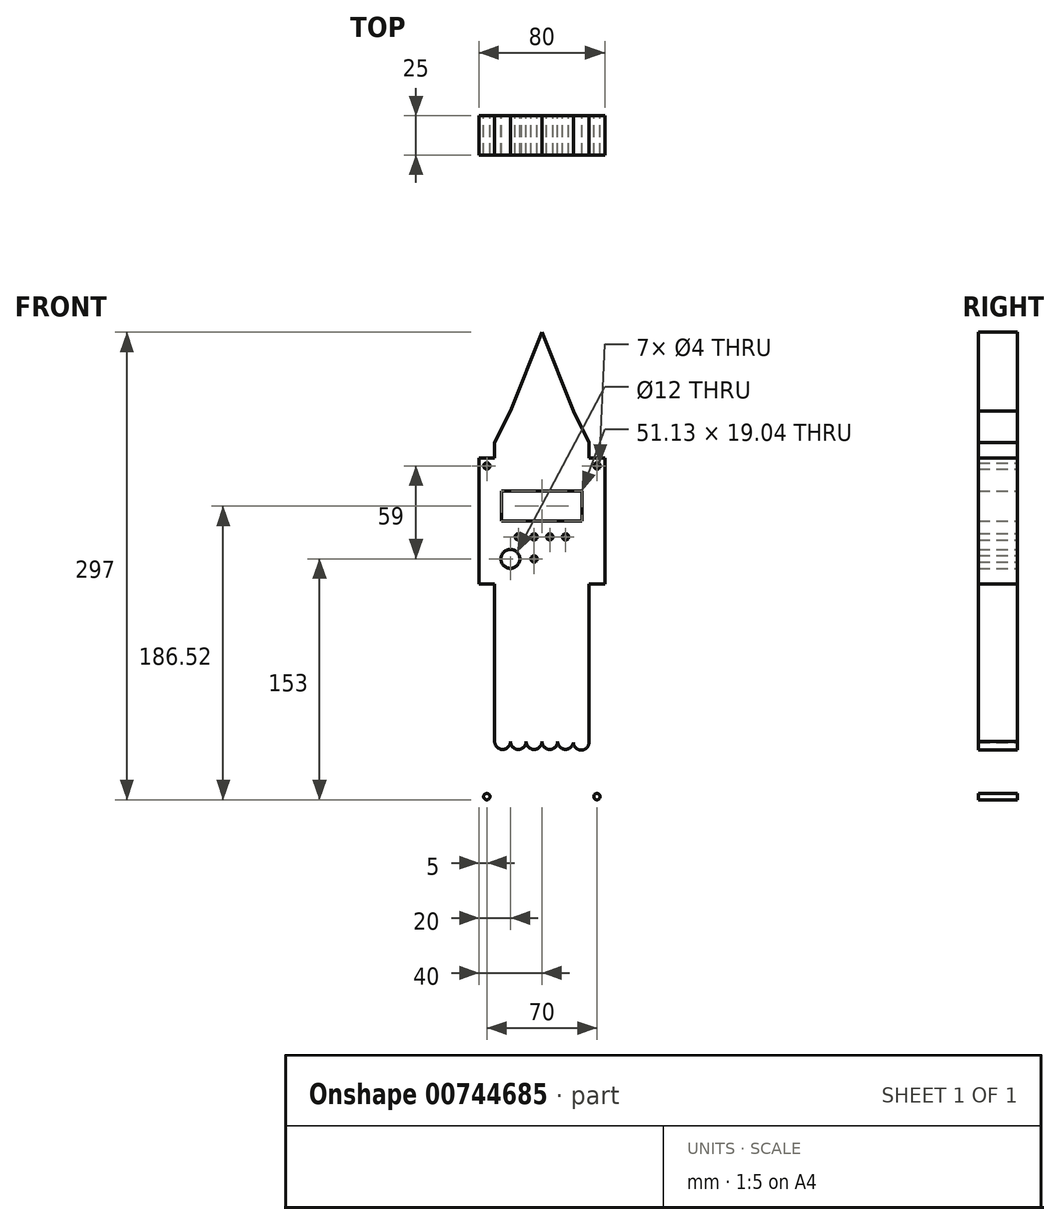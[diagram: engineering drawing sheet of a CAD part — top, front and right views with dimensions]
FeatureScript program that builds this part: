
annotation { "Feature Type Name" : "Feature", "Feature Type Description" : "" }
export const myFeature = defineFeature(function(context is Context, id is Id, definition is map)
    precondition{}
    {
        {
            var Q0;
            Q0=qCreatedBy(makeId("Front.planeOp"),FACE);
            var sketch = newSketch(context, id + "F0", { "sketchPlane" : qUnion([Q0])});
            skLineSegment(sketch, "E0", {"start": v(0, 0) * mm, "end": v(-40, 0) * mm});
            skLineSegment(sketch, "E1", {"start": v(-40, 0) * mm, "end": v(-40, 10) * mm});
            skLineSegment(sketch, "E2", {"start": v(-40, 10) * mm, "end": v(-30, 10) * mm});
            skLineSegment(sketch, "E3", {"start": v(-30, 10) * mm, "end": v(-30, 140) * mm});
            skLineSegment(sketch, "E4", {"start": v(-30, 140) * mm, "end": v(-40, 140) * mm});
            skLineSegment(sketch, "E5", {"start": v(-40, 140) * mm, "end": v(-40, 220) * mm});
            skLineSegment(sketch, "E6", {"start": v(-40, 220) * mm, "end": v(-30, 220) * mm});
            skLineSegment(sketch, "E7", {"start": v(-30, 220) * mm, "end": v(-30, 230) * mm});
            skLineSegment(sketch, "E8", {"start": v(-30, 230) * mm, "end": v(0, 230) * mm});
            skLineSegment(sketch, "E9", {"start": v(0, 250) * mm, "end": v(-20, 250) * mm});
            skLineSegment(sketch, "E10", {"start": v(-30, 230) * mm, "end": v(-20, 250) * mm});
            skLineSegment(sketch, "E11", {"start": v(-20, 250) * mm, "end": v(0, 300) * mm});
            skLineSegment(sketch, "E12.MirrorCS", {"start": v(39.95, 10) * mm, "end": v(29.95, 10) * mm});
            skLineSegment(sketch, "E13.MirrorCS", {"start": v(30, 140) * mm, "end": v(40, 140) * mm});
            skLineSegment(sketch, "E14.MirrorCS", {"start": v(40, 220) * mm, "end": v(30, 220) * mm});
            skLineSegment(sketch, "E15.MirrorCS", {"start": v(30, 220) * mm, "end": v(30, 230) * mm});
            skLineSegment(sketch, "E16.MirrorCS", {"start": v(39.95, 0) * mm, "end": v(39.95, 10) * mm});
            skLineSegment(sketch, "E17.MirrorCS", {"start": v(20, 250) * mm, "end": v(0, 300) * mm});
            skLineSegment(sketch, "E18.MirrorCS", {"start": v(30, 230) * mm, "end": v(20, 250) * mm});
            skLineSegment(sketch, "E19.MirrorCS", {"start": v(-0.05, 0) * mm, "end": v(39.95, 0) * mm});
            skLineSegment(sketch, "E20.MirrorCS", {"start": v(29.95, 10) * mm, "end": v(30, 140) * mm});
            skLineSegment(sketch, "E21.MirrorCS", {"start": v(30, 230) * mm, "end": v(0, 230) * mm});
            skLineSegment(sketch, "E22.MirrorCS", {"start": v(0, 250) * mm, "end": v(20, 250) * mm});
            skLineSegment(sketch, "E23.MirrorCS", {"start": v(40, 140) * mm, "end": v(40, 220) * mm});
            skLineSegment(sketch, "E24", {"start": v(-30, 140) * mm, "end": v(30, 140) * mm});
            skLineSegment(sketch, "E25", {"start": v(-30, 220) * mm, "end": v(30, 220) * mm});
            skLineSegment(sketch, "E26", {"start": v(-20, 140) * mm, "end": v(-20, 10) * mm});
            skLineSegment(sketch, "E27", {"start": v(-10, 140) * mm, "end": v(-10, 10.27) * mm});
            skLineSegment(sketch, "E28", {"start": v(0, 140) * mm, "end": v(0, 10) * mm});
            skLineSegment(sketch, "E29", {"start": v(10, 140) * mm, "end": v(10, 10) * mm});
            skLineSegment(sketch, "E30", {"start": v(20, 140) * mm, "end": v(20, 10) * mm});
            skArc(sketch, "E31", {"start": v(-30, 120) * mm, "mid": v(-25, 115) * mm, "end": v(-20, 120) * mm});
            skArc(sketch, "E32", {"start": v(-20, 120) * mm, "mid": v(-15, 115) * mm, "end": v(-10, 120) * mm});
            skArc(sketch, "E33", {"start": v(-10, 120) * mm, "mid": v(-5, 115) * mm, "end": v(0, 120) * mm});
            skArc(sketch, "E34", {"start": v(0, 120) * mm, "mid": v(5, 115) * mm, "end": v(10, 120) * mm});
            skArc(sketch, "E35", {"start": v(10, 120) * mm, "mid": v(15, 115) * mm, "end": v(20, 120) * mm});
            skArc(sketch, "E36", {"start": v(20, 120) * mm, "mid": v(25, 115.2) * mm, "end": v(30, 120) * mm});
            skArc(sketch, "E37", {"start": v(-30, 80) * mm, "mid": v(-25, 75) * mm, "end": v(-20, 80) * mm});
            skArc(sketch, "E38", {"start": v(-20, 80) * mm, "mid": v(-15, 75) * mm, "end": v(-10, 80) * mm});
            skArc(sketch, "E39", {"start": v(-10, 80) * mm, "mid": v(-5, 75) * mm, "end": v(0, 80) * mm});
            skArc(sketch, "E40", {"start": v(0, 80) * mm, "mid": v(5, 75) * mm, "end": v(10, 80) * mm});
            skArc(sketch, "E41", {"start": v(10, 80) * mm, "mid": v(15, 75) * mm, "end": v(20, 80) * mm});
            skArc(sketch, "E42", {"start": v(20, 80) * mm, "mid": v(24.99, 75.35) * mm, "end": v(29.97, 80) * mm});
            skArc(sketch, "E43", {"start": v(-30, 40) * mm, "mid": v(-25, 35) * mm, "end": v(-20, 40) * mm});
            skArc(sketch, "E44", {"start": v(-20, 40) * mm, "mid": v(-15, 35) * mm, "end": v(-10, 40) * mm});
            skArc(sketch, "E45", {"start": v(-10, 40) * mm, "mid": v(-5, 35) * mm, "end": v(0, 40) * mm});
            skArc(sketch, "E46", {"start": v(0, 40) * mm, "mid": v(5, 35) * mm, "end": v(10, 40) * mm});
            skArc(sketch, "E47", {"start": v(10, 40) * mm, "mid": v(15, 35) * mm, "end": v(20, 40) * mm});
            skArc(sketch, "E48", {"start": v(20, 40) * mm, "mid": v(24.98, 34.54) * mm, "end": v(29.96, 40) * mm});
            skCircle(sketch, "E49", {"center": v(15, 170) * mm, "radius": 2 * mm});
            skCircle(sketch, "E50", {"center": v(5, 170) * mm, "radius": 2 * mm});
            skCircle(sketch, "E51", {"center": v(-5, 170) * mm, "radius": 2 * mm});
            skCircle(sketch, "E52", {"center": v(-15, 170) * mm, "radius": 2 * mm});
            skCircle(sketch, "E53", {"center": v(-5, 156) * mm, "radius": 2 * mm});
            skLineSegment(sketch, "E54.bottom", {"start": v(-25.56, 199.04) * mm, "end": v(25.56, 199.04) * mm});
            skLineSegment(sketch, "E54.top", {"start": v(-25.57, 180) * mm, "end": v(25.56, 180) * mm});
            skLineSegment(sketch, "E54.left", {"start": v(-25.57, 199.04) * mm, "end": v(-25.57, 180) * mm});
            skLineSegment(sketch, "E54.right", {"start": v(25.56, 199.04) * mm, "end": v(25.56, 180) * mm});
            skCircle(sketch, "E55", {"center": v(-20, 156) * mm, "radius": 6 * mm});
            skCircle(sketch, "E56", {"center": v(-35, 5) * mm, "radius": 2 * mm});
            skCircle(sketch, "E57", {"center": v(34.95, 5) * mm, "radius": 2 * mm});
            skCircle(sketch, "E58", {"center": v(35, 215) * mm, "radius": 2 * mm});
            skCircle(sketch, "E59", {"center": v(-35, 215) * mm, "radius": 2 * mm});
            skSolve(sketch);
        }
        {
            var Q0;
            Q0 = qSketchRegion(id + "F0", true);
            var Q1;
            {var subQ0=sQuery(id+"F0.wireOp",EDGE,"E32");Q1=makeQuery(id+"F0.imprint","IMPRINT",FACE,{"disambiguationData":[TD([[makeQuery(id+"F0.imprint","IMPRINT",EDGE,{"derivedFrom":subQ0}),-1.0]])]});}
            var Q2;
            {var subQ0=sQuery(id+"F0.wireOp",EDGE,"E33");Q2=makeQuery(id+"F0.imprint","IMPRINT",FACE,{"disambiguationData":[TD([[makeQuery(id+"F0.imprint","IMPRINT",EDGE,{"derivedFrom":subQ0}),-1.0]])]});}
            var Q3;
            {var subQ0=sQuery(id+"F0.wireOp",EDGE,"E34");Q3=makeQuery(id+"F0.imprint","IMPRINT",FACE,{"disambiguationData":[TD([[makeQuery(id+"F0.imprint","IMPRINT",EDGE,{"derivedFrom":subQ0}),-1.0]])]});}
            var Q4;
            {var subQ0=sQuery(id+"F0.wireOp",EDGE,"E35");Q4=makeQuery(id+"F0.imprint","IMPRINT",FACE,{"disambiguationData":[TD([[makeQuery(id+"F0.imprint","IMPRINT",EDGE,{"derivedFrom":subQ0}),-1.0]])]});}
            var Q5;
            {var subQ5=sQuery(id+"F0.wireOp",EDGE,"E41");Q5=makeQuery(id+"F0.imprint","IMPRINT",FACE,{"disambiguationData":[TD([[makeQuery(id+"F0.imprint","IMPRINT",EDGE,{"derivedFrom":subQ5}),-1.0]])]});}
            var Q6;
            {var subQ0=sQuery(id+"F0.wireOp",EDGE,"E40");Q6=makeQuery(id+"F0.imprint","IMPRINT",FACE,{"disambiguationData":[TD([[makeQuery(id+"F0.imprint","IMPRINT",EDGE,{"derivedFrom":subQ0}),-1.0]])]});}
            var Q7;
            {var subQ0=sQuery(id+"F0.wireOp",EDGE,"E39");Q7=makeQuery(id+"F0.imprint","IMPRINT",FACE,{"disambiguationData":[TD([[makeQuery(id+"F0.imprint","IMPRINT",EDGE,{"derivedFrom":subQ0}),-1.0]])]});}
            var Q8;
            {var subQ0=sQuery(id+"F0.wireOp",EDGE,"E38");Q8=makeQuery(id+"F0.imprint","IMPRINT",FACE,{"disambiguationData":[TD([[makeQuery(id+"F0.imprint","IMPRINT",EDGE,{"derivedFrom":subQ0}),-1.0]])]});}
            var Q9;
            {var subQ5=sQuery(id+"F0.wireOp",EDGE,"E32");Q9=makeQuery(id+"F0.imprint","IMPRINT",FACE,{"disambiguationData":[TD([[makeQuery(id+"F0.imprint","IMPRINT",EDGE,{"derivedFrom":subQ5}),1.0]])]});}
            var Q10;
            {var subQ5=sQuery(id+"F0.wireOp",EDGE,"E33");Q10=makeQuery(id+"F0.imprint","IMPRINT",FACE,{"disambiguationData":[TD([[makeQuery(id+"F0.imprint","IMPRINT",EDGE,{"derivedFrom":subQ5}),1.0]])]});}
            var Q11;
            {var subQ5=sQuery(id+"F0.wireOp",EDGE,"E34");Q11=makeQuery(id+"F0.imprint","IMPRINT",FACE,{"disambiguationData":[TD([[makeQuery(id+"F0.imprint","IMPRINT",EDGE,{"derivedFrom":subQ5}),1.0]])]});}
            var Q12;
            {var subQ5=sQuery(id+"F0.wireOp",EDGE,"E35");Q12=makeQuery(id+"F0.imprint","IMPRINT",FACE,{"disambiguationData":[TD([[makeQuery(id+"F0.imprint","IMPRINT",EDGE,{"derivedFrom":subQ5}),1.0]])]});}
            extrude(context, id + "F1", {"entities" : qUnion([Q0, Q1, Q2, Q3, Q4, Q5, Q6, Q7, Q8, Q9, Q10, Q11, Q12]), "depth" : 25 * mm, "offsetDistance" : 25 * mm});
        }
    });
